FCSTD DOCUMENT  (FreeCAD 0.15R4671 (Git))
Label: base_1_with_frame
License: All rights reserved
LicenseURL: http://en.wikipedia.org/wiki/All_rights_reserved
objects: Sketcher::SketchObject×1
note: 1 computed .brp shape members not serialized (recipe doc carries the construction recipe); baked Part::Feature solids carry a one-line shape summary decoded from their .brp

FEATURE [Sketcher::SketchObject] Sketch
  sketch-geometry (41):
    g0: Circle CenterX=0 CenterY=170 CenterZ=0 NormalX=0 NormalY=0 NormalZ=1 Radius=32
    g1: Circle CenterX=0 CenterY=-170 CenterZ=0 NormalX=0 NormalY=0 NormalZ=1 Radius=32
    g2: LineSegment StartX=-161 StartY=-50 StartZ=0 EndX=-183 EndY=-50 EndZ=0
    g3: LineSegment StartX=-183 StartY=-50 StartZ=0 EndX=-183 EndY=50 EndZ=0
    g4: LineSegment StartX=-183 StartY=50 StartZ=0 EndX=-161 EndY=50 EndZ=0
    g5: LineSegment StartX=-161 StartY=50 StartZ=0 EndX=-161 EndY=-50 EndZ=0
    g6: LineSegment StartX=183 StartY=50 StartZ=0 EndX=161 EndY=50 EndZ=0
    g7: LineSegment StartX=161 StartY=50 StartZ=0 EndX=161 EndY=-50 EndZ=0
    g8: LineSegment StartX=161 StartY=-50 StartZ=0 EndX=183 EndY=-50 EndZ=0
    g9: LineSegment StartX=183 StartY=-50 StartZ=0 EndX=183 EndY=50 EndZ=0
    g10: Circle CenterX=-90 CenterY=172.291 CenterZ=0 NormalX=0 NormalY=0 NormalZ=1 Radius=2.5
    g11: Circle CenterX=90 CenterY=172.291 CenterZ=0 NormalX=0 NormalY=0 NormalZ=1 Radius=2.5
    g12: Circle CenterX=-30 CenterY=200 CenterZ=0 NormalX=0 NormalY=0 NormalZ=1 Radius=2.5
    g13: Circle CenterX=30 CenterY=200 CenterZ=0 NormalX=0 NormalY=0 NormalZ=1 Radius=2.5
    g14: Circle CenterX=-30 CenterY=140 CenterZ=0 NormalX=0 NormalY=0 NormalZ=1 Radius=2.5
    g15: Circle CenterX=30 CenterY=140 CenterZ=0 NormalX=0 NormalY=0 NormalZ=1 Radius=2.5
    g16: Circle CenterX=-30 CenterY=-140 CenterZ=0 NormalX=0 NormalY=0 NormalZ=1 Radius=2.5
    g17: Circle CenterX=30 CenterY=-140 CenterZ=0 NormalX=0 NormalY=0 NormalZ=1 Radius=2.5
    g18: Circle CenterX=-30 CenterY=-200 CenterZ=0 NormalX=0 NormalY=0 NormalZ=1 Radius=2.5
    g19: Circle CenterX=30 CenterY=-200 CenterZ=0 NormalX=0 NormalY=0 NormalZ=1 Radius=2.5
    g20: LineSegment StartX=-103 StartY=128 StartZ=0 EndX=103 EndY=128 EndZ=0
    g21: LineSegment StartX=103 StartY=128 StartZ=0 EndX=103 EndY=-128 EndZ=0
    g22: LineSegment StartX=103 StartY=-128 StartZ=0 EndX=-103 EndY=-128 EndZ=0
    g23: LineSegment StartX=-103 StartY=-128 StartZ=0 EndX=-103 EndY=128 EndZ=0
    g24: LineSegment StartX=-141 StartY=41 StartZ=0 EndX=-138 EndY=41 EndZ=0
    g25: LineSegment StartX=-138 StartY=41 StartZ=0 EndX=-138 EndY=-41 EndZ=0
    g26: LineSegment StartX=-138 StartY=-41 StartZ=0 EndX=-141 EndY=-41 EndZ=0
    g27: LineSegment StartX=-141 StartY=-41 StartZ=0 EndX=-141 EndY=41 EndZ=0
    g28: LineSegment StartX=138 StartY=41 StartZ=0 EndX=141 EndY=41 EndZ=0
    g29: LineSegment StartX=141 StartY=41 StartZ=0 EndX=141 EndY=-41 EndZ=0
    g30: LineSegment StartX=141 StartY=-41 StartZ=0 EndX=138 EndY=-41 EndZ=0
    g31: LineSegment StartX=138 StartY=-41 StartZ=0 EndX=138 EndY=41 EndZ=0
    g32: LineSegment StartX=207.873 StartY=-86.1038 StartZ=0 EndX=207.873 EndY=86.1038 EndZ=0
    g33: LineSegment StartX=207.873 StartY=86.1038 StartZ=0 EndX=86.1038 EndY=207.873 EndZ=0
    g34: LineSegment StartX=86.1038 StartY=207.873 StartZ=0 EndX=-86.1038 EndY=207.873 EndZ=0
    g35: LineSegment StartX=-86.1038 StartY=207.873 StartZ=0 EndX=-207.873 EndY=86.1038 EndZ=0
    g36: LineSegment StartX=-207.873 StartY=86.1038 StartZ=0 EndX=-207.873 EndY=-86.1038 EndZ=0
    g37: LineSegment StartX=-207.873 StartY=-86.1038 StartZ=0 EndX=-86.1038 EndY=-207.873 EndZ=0
    g38: LineSegment StartX=-86.1038 StartY=-207.873 StartZ=0 EndX=86.1038 EndY=-207.873 EndZ=0
    g39: LineSegment StartX=86.1038 StartY=-207.873 StartZ=0 EndX=207.873 EndY=-86.1038 EndZ=0
    g40: Circle [constr] CenterX=0 CenterY=0 CenterZ=0 NormalX=0 NormalY=0 NormalZ=1 Radius=225
  constraints (106):
    c: PointOnObject(g0,g-2)
    c: PointOnObject(g1,g-2)
    c: Equal(g1,g0)
    c: Coincident(g2,g3)
    c: Coincident(g3,g4)
    c: Coincident(g4,g5)
    c: Coincident(g5,g2)
    c: Horizontal(g2)
    c: Horizontal(g4)
    c: Vertical(g3)
    c: Vertical(g5)
    c: Coincident(g6,g7)
    c: Coincident(g7,g8)
    c: Coincident(g8,g9)
    c: Coincident(g9,g6)
    c: Horizontal(g6)
    c: Horizontal(g8)
    c: Vertical(g7)
    c: Vertical(g9)
    c: Equal(g5,g7)
    c: Equal(g6,g4)
    c: Symmetric(g6,g4,g-2)
    c: Symmetric(g11,g10,g-2)
    c: DistanceX(g-1,g10) = -90
    c: Radius(g12) = 2.5
    c: Symmetric(g12,g13,g-2)
    c: DistanceX(g-1,g12) = -30
    c: Equal(g12,g13)
    c: Symmetric(g15,g14,g-2)
    c: Equal(g19,g17)
    c: Equal(g17,g16)
    c: Equal(g16,g18)
    c: Equal(g18,g12)
    c: Symmetric(g18,g19,g-2)
    c: Symmetric(g17,g16,g-2)
    c: Symmetric(g14,g16,g-1)
    c: Symmetric(g12,g18,g-1)
    c: Equal(g10,g12)
    c: Equal(g11,g12)
    c: DistanceY(g3) = 100
    c: DistanceX(g2) = -22
    c: DistanceY(g14,g12) = 60
    c: DistanceX(g14,g15) = 60
    c: Symmetric(g4,g2,g-1)
    c: DistanceY(g-1,g0) = 170
    c: Symmetric(g1,g0,g-1)
    c: DistanceY(g13,g0) = -30
    c: Coincident(g20,g21)
    c: Coincident(g21,g22)
    c: Coincident(g22,g23)
    c: Coincident(g23,g20)
    c: Horizontal(g20)
    c: Horizontal(g22)
    c: Vertical(g21)
    c: Vertical(g23)
    c: DistanceY(g23) = 256
    c: DistanceX(g22) = -206
    c: Symmetric(g22,g21,g-2)
    c: Symmetric(g20,g22,g-1)
    c: Radius(g1) = 32
    c: DistanceX(g-1,g2) = -161
    c: Coincident(g24,g25)
    c: Coincident(g25,g26)
    c: Coincident(g26,g27)
    c: Coincident(g27,g24)
    c: Horizontal(g24)
    c: Horizontal(g26)
    c: Vertical(g25)
    c: Vertical(g27)
    c: DistanceY(g27) = 82
    c: DistanceX(g24) = 3
    c: DistanceX(g26,g2) = -20
    c: Symmetric(g24,g26,g-1)
    c: Coincident(g28,g29)
    c: Coincident(g29,g30)
    c: Coincident(g30,g31)
    c: Coincident(g31,g28)
    c: Horizontal(g28)
    c: Horizontal(g30)
    c: Vertical(g29)
    c: Vertical(g31)
    c: Equal(g31,g27)
    c: Equal(g28,g24)
    c: Symmetric(g28,g30,g-1)
    c: DistanceX(g29,g7) = 20
    c: Coincident(g32,g33)
    c: Coincident(g33,g34)
    c: Coincident(g34,g35)
    c: Coincident(g35,g36)
    c: Coincident(g36,g37)
    c: Coincident(g37,g38)
    c: Coincident(g38,g39)
    c: Coincident(g39,g32)
    c: Equal(g32, g33-g39) x7
    c: PointOnObject(g32,g40)
    c: PointOnObject(g33,g40)
    c: PointOnObject(g34,g40)
    c: PointOnObject(g35,g40)
    c: PointOnObject(g36,g40)
    c: PointOnObject(g37,g40)
    c: PointOnObject(g38,g40)
    c: PointOnObject(g39,g40)
    c: Coincident(g37,g-1)
    c: Radius(g40) = 225
    c: Coincident(g40,g-1)
    c: Vertical(g36)
